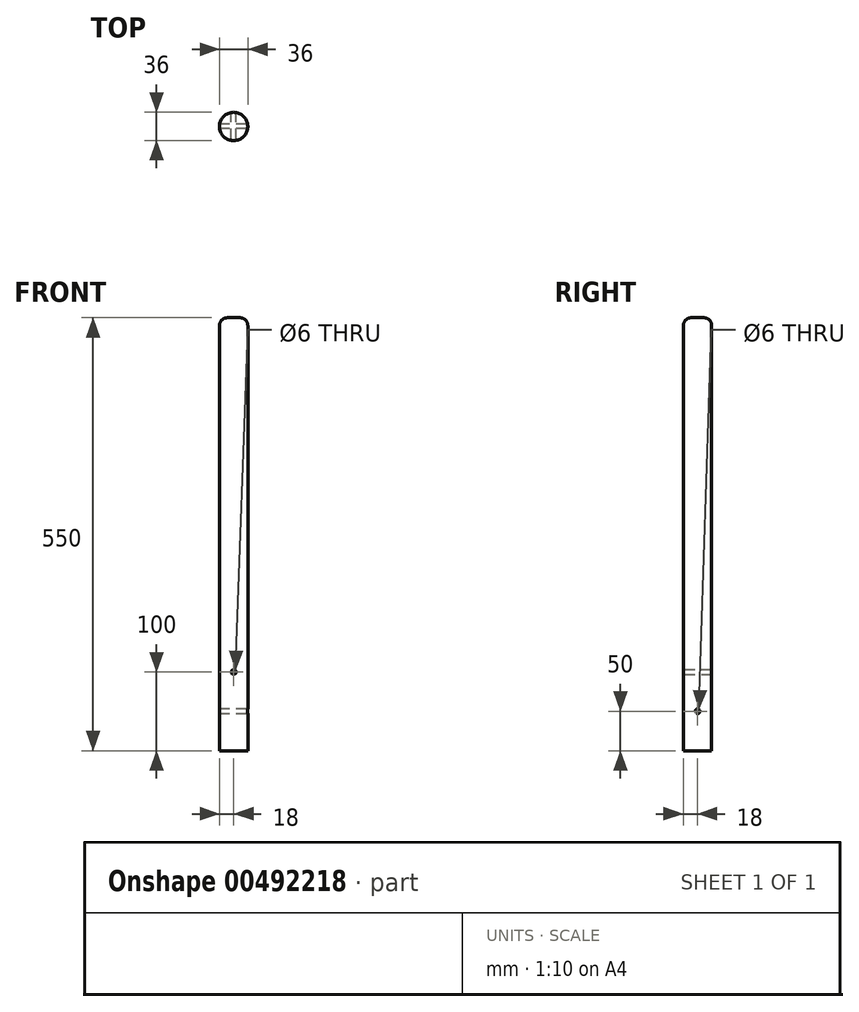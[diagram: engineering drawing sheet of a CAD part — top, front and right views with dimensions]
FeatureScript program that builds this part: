
annotation { "Feature Type Name" : "Feature", "Feature Type Description" : "" }
export const myFeature = defineFeature(function(context is Context, id is Id, definition is map)
    precondition{}
    {
        {
            var Q0;
            Q0=qCreatedBy(makeId("Top.planeOp"),FACE);
            var sketch = newSketch(context, id + "F0", { "sketchPlane" : qUnion([Q0])});
            skCircle(sketch, "E0", {"center": v(0, 0) * mm, "radius": 18 * mm});
            skSolve(sketch);
        }
        {
            var Q0;
            Q0 = qSketchRegion(id + "F0", true);
            extrude(context, id + "F1", {"entities" : qUnion([Q0]), "depth" : 550 * mm});
        }
        {
            var Q0;
            Q0=makeQuery(id+"F1.opExtrude","CAP_EDGE",EDGE,{"disambiguationData":[OSD([sQuery(id+"F0.wireOp",EDGE,"E0")])],"isStart":false});
            fillet(context, id + "F2", {"entities" : qUnion([Q0]), "radius" : 10 * mm, "tangentPropagation" : true, "allowEdgeOverflow" : false});
        }
        {
            var Q0;
            Q0=qCreatedBy(makeId("Front.planeOp"),FACE);
            var sketch = newSketch(context, id + "F3", { "sketchPlane" : qUnion([Q0])});
            skCircle(sketch, "E1", {"center": v(0, 100) * mm, "radius": 3 * mm});
            skSolve(sketch);
        }
        {
            var Q0;
            Q0=sQuery(id+"F3.wireOp",VERTEX,"E1.center");
            var Q1;
            Q1=makeQuery(id+"F1.opExtrude","SWEPT_BODY",BODY,{"disambiguationData":[OSD([sQuery(id+"F0.wireOp",EDGE,"E0")])]});
            hole(context, id + "F4", {"style" : HoleStyle.SIMPLE, "endStyle" : HoleEndStyle.THROUGH, "oppositeDirection" : true, "holeDiameter" : 6 * mm, "isTappedThrough" : true, "tappedDepth" : 12 * mm, "tapClearance" : 3, "startFromSketch" : true, "locations" : qUnion([Q0]), "scope" : qUnion([Q1])});
        }
        {
            var Q0;
            Q0=sQuery(id+"F3.wireOp",VERTEX,"E1.center");
            var Q1;
            Q1=makeQuery(id+"F1.opExtrude","SWEPT_BODY",BODY,{"disambiguationData":[OSD([sQuery(id+"F0.wireOp",EDGE,"E0")])]});
            hole(context, id + "F5", {"style" : HoleStyle.SIMPLE, "endStyle" : HoleEndStyle.THROUGH, "holeDiameter" : 6 * mm, "isTappedThrough" : true, "tappedDepth" : 12 * mm, "tapClearance" : 3, "startFromSketch" : true, "locations" : qUnion([Q0]), "scope" : qUnion([Q1])});
        }
        {
            var Q0;
            Q0=qCreatedBy(makeId("Right.planeOp"),FACE);
            var sketch = newSketch(context, id + "F6", { "sketchPlane" : qUnion([Q0])});
            skCircle(sketch, "E2", {"center": v(0, 50) * mm, "radius": 3 * mm});
            skSolve(sketch);
        }
        {
            var Q0;
            Q0=sQuery(id+"F6.wireOp",VERTEX,"E2.center");
            var Q1;
            Q1=makeQuery(id+"F1.opExtrude","SWEPT_BODY",BODY,{"disambiguationData":[OSD([sQuery(id+"F0.wireOp",EDGE,"E0")])]});
            hole(context, id + "F7", {"style" : HoleStyle.SIMPLE, "endStyle" : HoleEndStyle.THROUGH, "oppositeDirection" : true, "holeDiameter" : 6 * mm, "isTappedThrough" : true, "tappedDepth" : 12 * mm, "tapClearance" : 3, "startFromSketch" : true, "locations" : qUnion([Q0]), "scope" : qUnion([Q1])});
        }
        {
            var Q0;
            Q0=sQuery(id+"F6.wireOp",VERTEX,"E2.center");
            var Q1;
            Q1=makeQuery(id+"F1.opExtrude","SWEPT_BODY",BODY,{"disambiguationData":[OSD([sQuery(id+"F0.wireOp",EDGE,"E0")])]});
            hole(context, id + "F8", {"style" : HoleStyle.SIMPLE, "endStyle" : HoleEndStyle.THROUGH, "holeDiameter" : 6 * mm, "isTappedThrough" : true, "tappedDepth" : 12 * mm, "tapClearance" : 3, "startFromSketch" : true, "locations" : qUnion([Q0]), "scope" : qUnion([Q1])});
        }
    });
